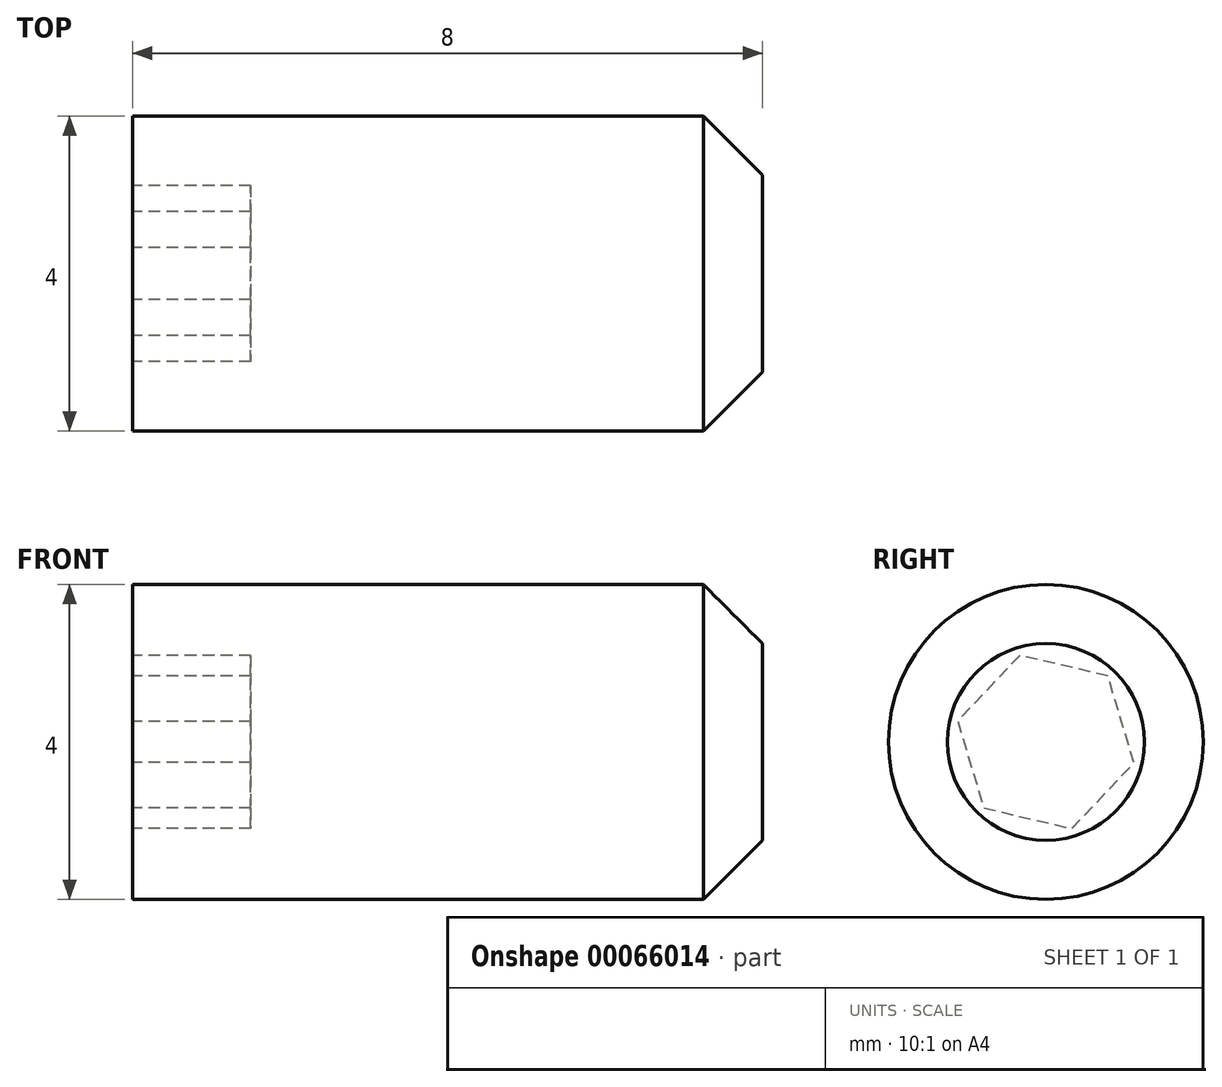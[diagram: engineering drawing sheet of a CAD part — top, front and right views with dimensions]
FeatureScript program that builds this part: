
annotation { "Feature Type Name" : "Feature", "Feature Type Description" : "" }
export const myFeature = defineFeature(function(context is Context, id is Id, definition is map)
    precondition{}
    {
        {
            var Q0;
            Q0=qCreatedBy(makeId("Front.planeOp"),FACE);
            var sketch = newSketch(context, id + "F0", { "sketchPlane" : qUnion([Q0])});
            skLineSegment(sketch, "E0.bottom", {"start": v(-4, 2) * mm, "end": v(3.25, 2) * mm});
            skLineSegment(sketch, "E0.top", {"start": v(-4, 0) * mm, "end": v(4, 0) * mm});
            skLineSegment(sketch, "E0.left", {"start": v(-4, 2) * mm, "end": v(-4, 0) * mm});
            skLineSegment(sketch, "E0.right", {"start": v(4, 1.25) * mm, "end": v(4, 0) * mm});
            skLineSegment(sketch, "E1", {"start": v(3.25, 2) * mm, "end": v(4, 1.25) * mm});
            skSolve(sketch);
        }
        {
            var Q0;
            Q0=makeQuery(id+"F0.imprint","IMPRINT",FACE,{"disambiguationData":[TD([[makeQuery(id+"F0.imprint","IMPRINT",EDGE,{"derivedFrom":sQuery(id+"F0.wireOp",EDGE,"E0.bottom")}),-1.0]])]});
            var Q1;
            Q1=sQuery(id+"F0.wireOp",EDGE,"E0.top");
            revolve(context, id + "F1", {"entities" : qUnion([Q0]), "axis" : qUnion([Q1]), "revolveType" : RevolveType.FULL});
        }
        {
            var Q0;
            Q0=makeQuery(id+"F1.opRevolve","SWEPT_FACE",FACE,{"disambiguationData":[OSD([sQuery(id+"F0.wireOp",EDGE,"E0.left")])]});
            var sketch = newSketch(context, id + "F2", { "sketchPlane" : qUnion([Q0])});
            skCircle(sketch, "E2.cCircle", {"center": v(0, 0) * mm, "radius": 1.15 * mm, "construction": true});
            skLineSegment(sketch, "E2.0", {"start": v(0.33, 1.1) * mm, "end": v(1.12, 0.26) * mm});
            skLineSegment(sketch, "E2.1", {"start": v(1.12, 0.26) * mm, "end": v(0.79, -0.84) * mm});
            skLineSegment(sketch, "E2.2", {"start": v(0.79, -0.84) * mm, "end": v(-0.33, -1.1) * mm});
            skLineSegment(sketch, "E2.3", {"start": v(-0.33, -1.1) * mm, "end": v(-1.12, -0.26) * mm});
            skLineSegment(sketch, "E2.4", {"start": v(-1.12, -0.26) * mm, "end": v(-0.79, 0.84) * mm});
            skLineSegment(sketch, "E2.5", {"start": v(-0.79, 0.84) * mm, "end": v(0.33, 1.1) * mm});
            skSolve(sketch);
        }
        {
            var Q0;
            Q0=makeQuery(id+"F2.imprint","IMPRINT",FACE,{"disambiguationData":[TD([[makeQuery(id+"F2.imprint","IMPRINT",EDGE,{"derivedFrom":sQuery(id+"F2.wireOp",EDGE,"E2.0")}),-1.0]])]});
            extrude(context, id + "F3", {"entities" : qUnion([Q0]), "operationType" : NewBodyOperationType.REMOVE, "oppositeDirection" : true, "depth" : 1.5 * mm});
        }
    });
